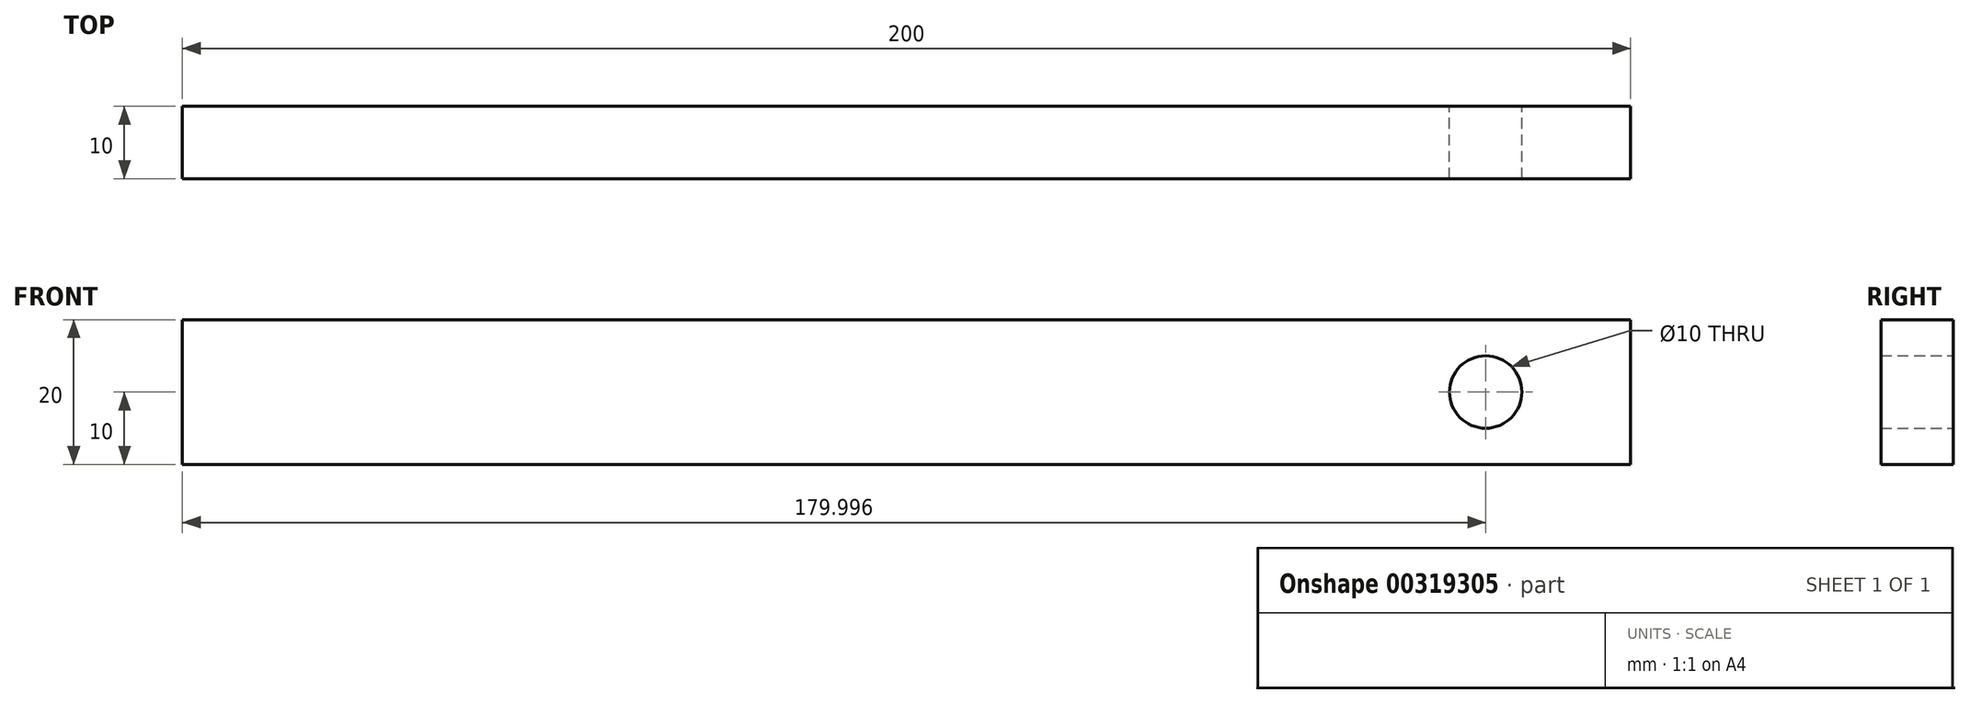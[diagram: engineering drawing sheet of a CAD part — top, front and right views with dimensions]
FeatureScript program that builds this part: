
annotation { "Feature Type Name" : "Feature", "Feature Type Description" : "" }
export const myFeature = defineFeature(function(context is Context, id is Id, definition is map)
    precondition{}
    {
        {
            var Q0;
            Q0=qCreatedBy(makeId("Front.planeOp"),FACE);
            var sketch = newSketch(context, id + "F0", { "sketchPlane" : qUnion([Q0])});
            skLineSegment(sketch, "E0.bottom", {"start": v(-85.01, 0) * mm, "end": v(114.99, 0) * mm});
            skLineSegment(sketch, "E0.top", {"start": v(-85.01, 20) * mm, "end": v(114.99, 20) * mm});
            skLineSegment(sketch, "E0.left", {"start": v(-85.01, 0) * mm, "end": v(-85.01, 20) * mm});
            skLineSegment(sketch, "E0.right", {"start": v(114.99, 0) * mm, "end": v(114.99, 20) * mm});
            skCircle(sketch, "E1", {"center": v(94.99, 10) * mm, "radius": 5 * mm});
            skSolve(sketch);
        }
        {
            var Q0;
            Q0 = qSketchRegion(id + "F0", true);
            extrude(context, id + "F1", {"entities" : qUnion([Q0]), "depth" : 10 * mm});
        }
    });
